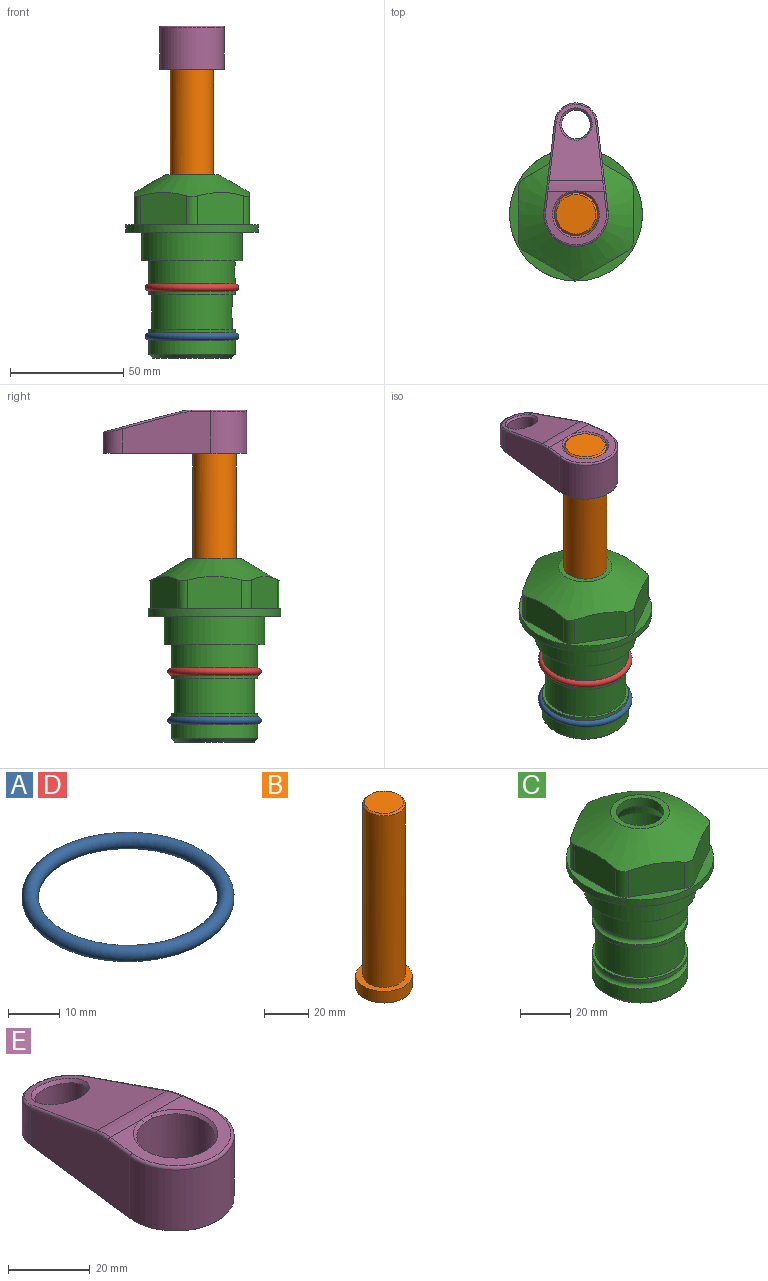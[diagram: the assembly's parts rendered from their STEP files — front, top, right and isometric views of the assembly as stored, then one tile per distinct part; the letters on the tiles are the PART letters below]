
ASSEMBLY  parts=5 mates=4
PART A: 1 faces, bbox 44.7x44.7x3.2 mm
  f0: torus R=19.05mm, axis (0,0,1), area 1193.9mm2
PART B: 6 faces, bbox 25.4x25.4x101.6 mm
  f0: plane 17.46x17.46mm, normal (0,0,1), area 239.5mm2, adj f5
  f1: plane 25.4x25.4mm, normal (0,0,-1), area 506.7mm2, adj f2
  f2: cylinder r=12.7mm len=25.4mm, axis (0,0,1), area 506.7mm2, adj f1,f3
  f3: plane 25.4x25.4mm, normal (0,0,1), area 221.7mm2, adj f2,f4
  f4: cylinder r=9.53mm len=94.46mm, axis (0,0,1), area 5653mm2, adj f3,f5
  f5: cone r=8.73mm half-angle=45deg, axis (0,0,-1), area 64.4mm2, adj f0,f4
PART C: 36 faces, bbox 58.7x58.7x81 mm
  f0: cylinder r=17.78mm len=35.56mm, axis (0,0,1), area 1670.8mm2, adj f23,f24,f31
  f1: cylinder r=19.05mm len=38.1mm, axis (0,0,1), area 1191.9mm2, adj f26,f27,f30
  f2: plane 58.66x58.66mm, normal (0,0,-1), area 1150.6mm2, adj f3,f28
  f3: cylinder r=29.33mm len=58.66mm, axis (0,0,-1), area 585.1mm2, adj f2,f4
  f4: plane 58.66x58.66mm, normal (0,0,1), area 475.9mm2, adj f3,f5,f6,f7,f8,f9,f10,f11
  f5: plane 20.32x14.34mm, normal (-0.5,0.87,0), area 324.4mm2, adj f4,f15,f16,f17
  f6: plane 20.32x14.34mm, normal (0.5,0.87,0), area 324.4mm2, adj f4,f14,f15,f17
  f7: plane 23.48x14.34mm, normal (1,0,0), area 324.4mm2, adj f4,f13,f14,f17
  f8: plane 20.32x14.34mm, normal (0.5,-0.87,0), area 324.4mm2, adj f4,f12,f13,f17
  f9: plane 20.32x14.34mm, normal (-0.5,-0.87,0), area 324.4mm2, adj f4,f11,f12,f17
  f10: plane 23.48x14.34mm, normal (-1,0,0), area 324.4mm2, adj f4,f11,f16,f17
  f11: cylinder r=5.08mm len=12.85mm, axis (0,0,-1), area 67.2mm2, adj f4,f9,f10,f17
  f12: cylinder r=5.08mm len=12.85mm, axis (0,0,-1), area 67.2mm2, adj f4,f8,f9,f17
  f13: cylinder r=5.08mm len=12.85mm, axis (0,0,-1), area 67.2mm2, adj f4,f7,f8,f17
  f14: cylinder r=5.08mm len=12.85mm, axis (0,0,-1), area 67.2mm2, adj f4,f6,f7,f17
  f15: cylinder r=5.08mm len=12.85mm, axis (0,0,-1), area 67.2mm2, adj f4,f5,f6,f17
  f16: cylinder r=5.08mm len=12.85mm, axis (0,0,-1), area 67.2mm2, adj f4,f5,f10,f17
  f17: cone r=11.73mm half-angle=60deg, axis (0,0,-1), area 2071.8mm2, adj f5,f6,f7,f8,f9,f10,f11,f12
  f18: plane 23.46x23.46mm, normal (0,0,1), area 147.4mm2, adj f17,f35
  f19: plane 34.93x34.93mm, normal (0,0,-1), area 958mm2, adj f29
  f20: cylinder r=19.05mm len=38.1mm, axis (0,0,1), area 760.1mm2, adj f21,f29
  f21: torus R=19.05mm, axis (0,0,1), area 565.3mm2, adj f20,f22
  f22: cylinder r=19.05mm len=38.1mm, axis (0,0,1), area 190mm2, adj f21,f23
  f23: plane 38.1x38.1mm, normal (0,0,1), area 146.9mm2, adj f0,f22
  f24: plane 38.1x38.1mm, normal (0,0,-1), area 146.9mm2, adj f0,f25
  f25: cylinder r=19.05mm len=38.1mm, axis (0,0,1), area 190mm2, adj f24,f26
  f26: torus R=19.05mm, axis (0,0,1), area 565.3mm2, adj f1,f25
  f27: plane 44.45x44.45mm, normal (0,0,-1), area 411.7mm2, adj f1,f28
  f28: cylinder r=22.23mm len=44.45mm, axis (0,0,1), area 1773.5mm2, adj f2,f27
  f29: cone r=19.05mm half-angle=45deg, axis (0,0,1), area 257.5mm2, adj f19,f20
  f30: cylinder r=3.17mm len=6.75mm, axis (-1,0,0), area 128mm2, adj f1,f33
  f31: cylinder r=3.17mm len=6.35mm, axis (-1,0,0), area 102.5mm2, adj f0,f33
  f32: plane 25.4x25.4mm, normal (0,0,1), area 506.7mm2, adj f33
  f33: cylinder r=12.7mm len=66.42mm, axis (0,0,-1), area 5236.2mm2, adj f30,f31,f32,f34
  f34: cone r=9.53mm half-angle=30deg, axis (0,0,-1), area 443.4mm2, adj f33,f35
  f35: cylinder r=9.53mm len=19.05mm, axis (0,0,-1), area 240.9mm2, adj f18,f34
PART D: same geometry as A
PART E: 31 faces, bbox 31.7x65.5x19.8 mm
  f0: plane 39.12x18.26mm, normal (0.99,0.12,0), area 612.2mm2, adj f1,f4,f7,f11,f13,f15
  f1: cylinder r=9.53mm len=18.91mm, axis (0,0,-1), area 296.1mm2, adj f0,f2,f7,f17
  f2: plane 39.12x18.26mm, normal (-0.99,0.12,0), area 612.2mm2, adj f1,f4,f7,f12,f14,f16
  f3: cylinder r=6.35mm len=12.7mm, axis (0,0,-1), area 362.4mm2, adj f7,f18
  f4: cylinder r=14.29mm len=28.58mm, axis (0,0,-1), area 882.2mm2, adj f0,f2,f7,f10
  f5: cylinder r=9.53mm len=19.05mm, axis (0,0,-1), area 1092.6mm2, adj f7,f19,f20
  f6: plane 26.99x23.69mm, normal (0,0,1), area 216.2mm2, adj f9,f10,f11,f12,f19
  f7: plane 63.5x28.58mm, normal (0,0,-1), area 661.8mm2, adj f0,f1,f2,f3,f4,f5,f22,f23
  f8: plane 33.52x23.6mm, normal (0,0.26,0.97), area 486mm2, adj f9,f15,f16,f17,f18
  f9: cylinder r=19.05mm len=24.72mm, axis (1,0,0), area 120.4mm2, adj f6,f8,f13,f14,f20
  f10: torus R=13.49mm, axis (0,0,1), area 59mm2, adj f4,f6,f11,f12
  f11: cylinder r=0.79mm len=8.67mm, axis (0.12,-0.99,0), area 10.8mm2, adj f0,f6,f10,f13
  f12: cylinder r=0.79mm len=8.67mm, axis (0.12,0.99,0), area 10.8mm2, adj f2,f6,f10,f14
  f13: bspline ~4.95x1.42mm, area 6.1mm2, adj f0,f9,f11,f15
  f14: bspline ~4.95x1.42mm, area 6.1mm2, adj f2,f9,f12,f16
  f15: cylinder r=0.79mm len=25.95mm, axis (0.12,-0.96,0.26), area 32.9mm2, adj f0,f8,f13,f17
  f16: cylinder r=0.79mm len=25.95mm, axis (0.12,0.96,-0.26), area 32.9mm2, adj f2,f8,f14,f17
  f17: bspline ~18.91x8.38mm, area 30mm2, adj f1,f8,f15,f16
  f18: bspline ~14.29x14.29mm, area 48.3mm2, adj f3,f8
  f19: cone r=9.53mm half-angle=45deg, axis (0,0,1), area 66.5mm2, adj f5,f6,f20
  f20: bspline ~3.22x0.96mm, area 3.5mm2, adj f5,f9,f19
  f21: plane 2.75x2.72mm, normal (0,0,-1), area 2.9mm2, adj f23,f25,f28
  f22: plane 23.05x15.88mm, normal (-0.99,-0.12,0), area 323.6mm2, adj f7,f25,f26,f27,f28,f29
  f23: plane 23.05x15.88mm, normal (0.99,-0.12,0), area 323.6mm2, adj f7,f21,f25,f27,f28,f30
  f24: cylinder r=9.53mm len=10.69mm, axis (0,0,-1), area 114.7mm2, adj f7,f27,f29,f30
  f25: cylinder r=12.7mm len=20.59mm, axis (0,0,-1), area 381.1mm2, adj f7,f21,f22,f23,f26,f28
  f26: plane 2.75x2.72mm, normal (0,0,-1), area 2.9mm2, adj f22,f25,f28
  f27: plane 19.72x18.37mm, normal (0,-0.26,-0.97), area 291.8mm2, adj f22,f23,f24,f28,f29,f30
  f28: cylinder r=15.88mm len=19.92mm, axis (1,0,0), area 54.8mm2, adj f21,f22,f23,f25,f26,f27
  f29: cylinder r=1.59mm len=11mm, axis (0,0,-1), area 34.7mm2, adj f7,f22,f24,f27
  f30: cylinder r=1.59mm len=11mm, axis (0,0,-1), area 34.7mm2, adj f7,f23,f24,f27
PLACE A t=(0,0,-21.59)mm
PLACE B t=(0,0,27.55)mm
PLACE C at identity fixed
PLACE D at identity
PLACE E t=(0,0,27.55)mm
MATE cylindrical B.f2 <-> C.f0  axis (0,0,-1) through (0,0,-10.55)mm
MATE fastened A.f0 <-> C.f0  axis (0,0,1) through (0,0,-46.1)mm
MATE fastened B.f2 <-> E.f4  axis (0,0,-1) through (0,0,90.26)mm
MATE fastened C.f0 <-> D.f0  axis (0,0,1) through (0,0,-24.51)mm
